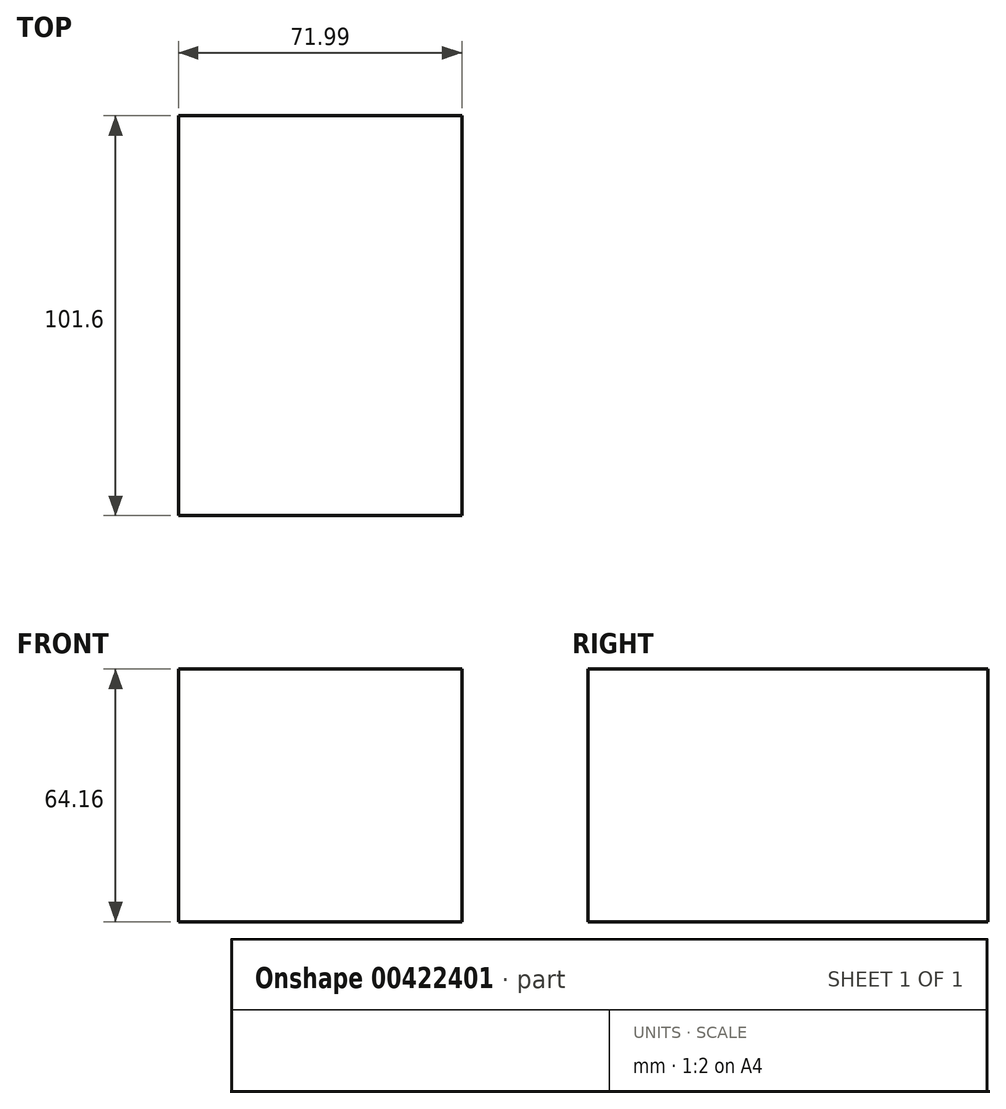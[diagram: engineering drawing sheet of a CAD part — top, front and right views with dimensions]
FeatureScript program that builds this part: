
annotation { "Feature Type Name" : "Feature", "Feature Type Description" : "" }
export const myFeature = defineFeature(function(context is Context, id is Id, definition is map)
    precondition{}
    {
        {
            var Q0;
            Q0=qCreatedBy(makeId("Front.planeOp"),FACE);
            var sketch = newSketch(context, id + "F0", { "sketchPlane" : qUnion([Q0])});
            skLineSegment(sketch, "E0.bottom", {"start": v(0, 0) * mm, "end": v(-71.99, 0) * mm});
            skLineSegment(sketch, "E0.top", {"start": v(0, 64.16) * mm, "end": v(-71.99, 64.16) * mm});
            skLineSegment(sketch, "E0.left", {"start": v(0, 0) * mm, "end": v(0, 64.16) * mm});
            skLineSegment(sketch, "E0.right", {"start": v(-71.99, 0) * mm, "end": v(-71.99, 64.16) * mm});
            skSolve(sketch);
        }
        {
            var Q0;
            Q0=makeQuery(id+"F0.imprint","IMPRINT",FACE,{"disambiguationData":[TD([[makeQuery(id+"F0.imprint","IMPRINT",EDGE,{"derivedFrom":sQuery(id+"F0.wireOp",EDGE,"E0.bottom")}),-1.0]])]});
            extrude(context, id + "F1", {"entities" : qUnion([Q0]), "depth" : 101.6 * mm});
        }
    });
